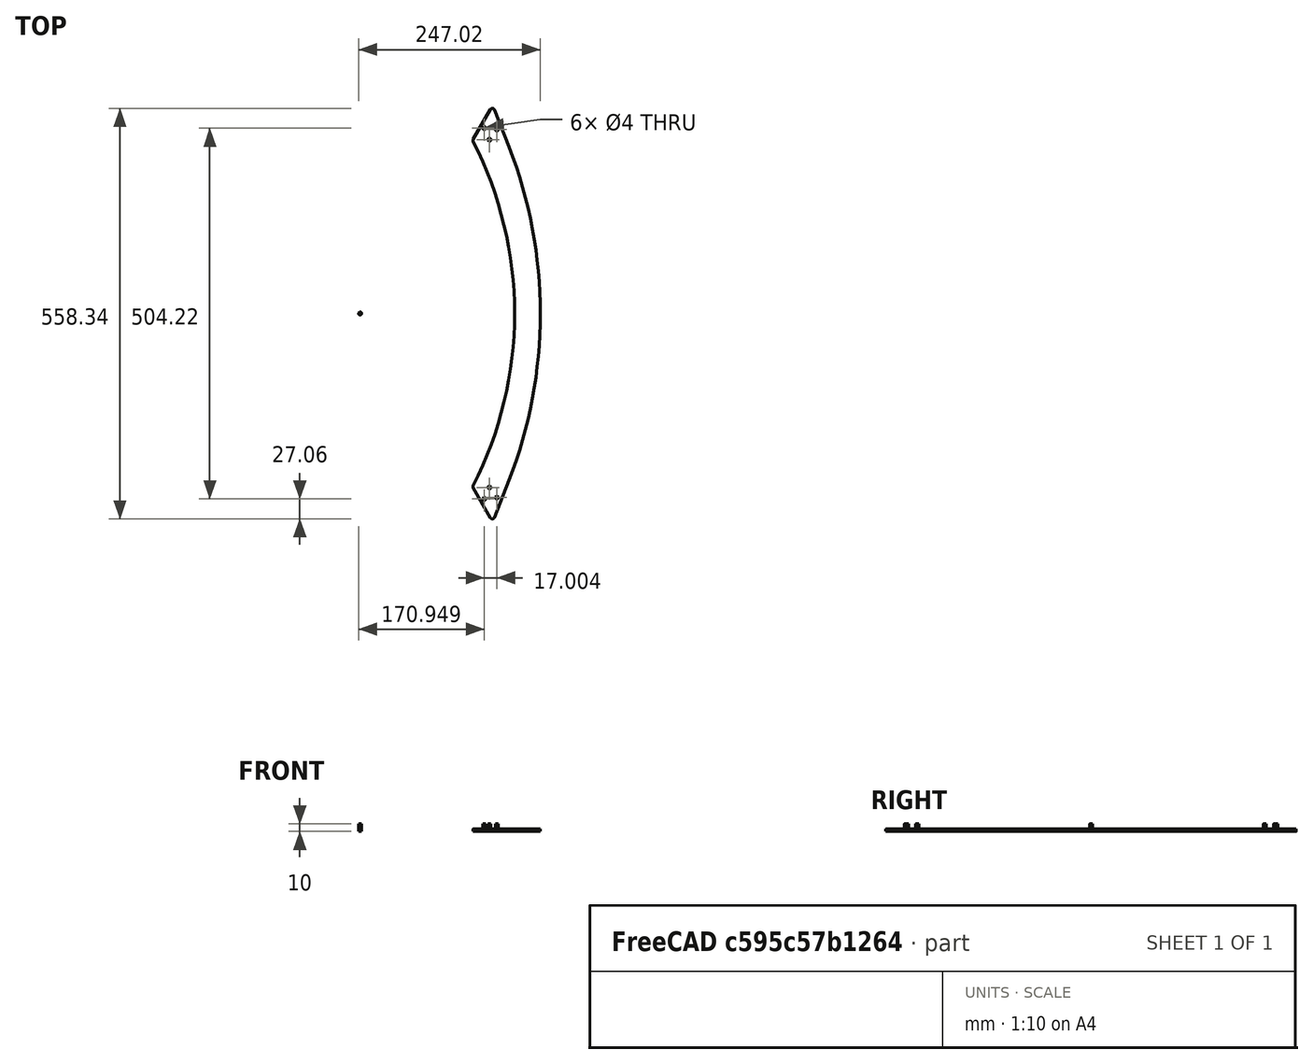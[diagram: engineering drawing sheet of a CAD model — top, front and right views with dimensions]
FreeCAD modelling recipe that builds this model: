
FCSTD DOCUMENT  (FreeCAD 1.1R38827 (Git))
Label: composit_stand3_tech_sector_hor_model
License: All rights reserved
LicenseURL: http://en.wikipedia.org/wiki/All_rights_reserved
objects: Part::FeaturePython×5, App::Link×3, PartDesign::SubShapeBinder×2, PartDesign::Body×2, PartDesign::CoordinateSystem×2, Part::Mirroring×1, PartDesign::Pad×1, Part::Cylinder×1, Part::MultiFuse×1, PartDesign::Boolean×1
note: 19 computed .brp shape members not serialized (recipe doc carries the construction recipe); baked Part::Feature solids carry a one-line shape summary decoded from their .brp
EXTERNAL_REF file=composit_stand3_tech_sector_hor_main.FCStd obj=Sketch
EXTERNAL_REF file=composit_stand3_tech_sector_plexiglass_main.FCStd obj=Placment
EXTERNAL_REF file=composit_stand3_tech_sector_hor_main.FCStd obj=Link001
EXTERNAL_REF file=composit_stand3_tech_sector_pillar_main.FCStd obj=ArrayFromShape

FEATURE [PartDesign::SubShapeBinder] Binder
  BindCopyOnChange = 0
  BindMode = 0
  ClaimChildren = true
  Fuse = false
  MakeFace = true
  OffsetFill = false
  OffsetIntersection = false
  OffsetJoinType = 0
  OffsetOpenResult = false
  PartialLoad = false
  Relative = true
  Support = -> [<external composit_stand3_tech_sector_hor_main.FCStd>#Sketch]
  _Version = 2
FEATURE [Part::Mirroring] Part__Mirroring  label="Binder (Mirror #1)"
  Base = (0,0,0)
  Normal = (0,1,0)
  Source = -> Binder
FEATURE [Part::FeaturePython] Connect  # WARN: FeaturePython — macro-defined, semantics opaque (R4)
  Objects = -> [Binder,Part__Mirroring]
  Tolerance = 0
FEATURE [PartDesign::SubShapeBinder] Binder001
  BindCopyOnChange = 0
  BindMode = 0
  ClaimChildren = true
  Context = -> Body [Binder001.]
  Fuse = false
  MakeFace = true
  OffsetFill = false
  OffsetIntersection = false
  OffsetJoinType = 0
  OffsetOpenResult = false
  PartialLoad = false
  Relative = false
  Support = -> [Connect]
  _Version = 2
FEATURE [PartDesign::Pad] Pad
  Direction = (0,0,1)
  Length = 3
  Length2 = 10
  Profile = -> Binder001
  Suppressed = false
  Type = 0
FEATURE [App::Link] Link001  label="edge_placement"
  LinkTransform = true
  LinkedObject = -> <external composit_stand3_tech_sector_plexiglass_main.FCStd>#Placment
FEATURE [App::Link] Link002  label="front_support_intersection_placement"
  LinkedObject = -> <external composit_stand3_tech_sector_hor_main.FCStd>#Link001
FEATURE [App::Link] Link003  label="holes_bottom"
  LinkedObject = -> <external composit_stand3_tech_sector_pillar_main.FCStd>#ArrayFromShape
FEATURE [Part::FeaturePython] Populate  label="Populate edge_placement with holes"  # WARN: FeaturePython — macro-defined, semantics opaque (R4)
  Copying = 0
  ExposePlacement = false
  MarkerShape = 1
  MarkerSize = 0
  NumElements = 3
  Object = -> Link003
  OutputCompounding = 0
  PlacementsFrom = -> Link002
  PlacementsTo = -> Link001
  Referencing = 3
  Type = lattice2PopulateCopies.LatticePopulateCopies
  isLattice = 1
FEATURE [Part::FeaturePython] Mirror  label="Mirror of Populate edge_placement with holes"  # WARN: FeaturePython — macro-defined, semantics opaque (R4)
  ExposePlacement = false
  FlipX = false
  FlipY = true
  FlipZ = false
  MarkerShape = 1
  MarkerSize = 0
  NumElements = 3
  Object = -> Populate
  ObjectTraversal = 0
  Type = lattice2Mirror.LatticeMirror
  isLattice = 1
FEATURE [Part::FeaturePython] Join  # WARN: FeaturePython — macro-defined, semantics opaque (R4)
  ExposePlacement = false
  Interleave = false
  Links = -> [Populate,Mirror]
  MarkerShape = 1
  MarkerSize = 0
  NumElements = 6
  Type = lattice2JoinArrays.JoinArrays
  isLattice = 1
FEATURE [Part::Cylinder] Cylinder  label="hole_3.4mm"
  Angle = 360
  AttacherType = Attacher::AttachEngine3D
  FirstAngle = 0
  Height = 10
  Radius = 2
  SecondAngle = 0
FEATURE [Part::FeaturePython] Populate001  label="Populate Join with hole_3.4mm"  # WARN: FeaturePython — macro-defined, semantics opaque (R4)
  Copying = 0
  ExposePlacement = false
  MarkerShape = 1
  MarkerSize = 0
  NumElements = 0
  Object = -> Cylinder
  OutputCompounding = 1
  PlacementsTo = -> Join
  Referencing = 0
  Type = lattice2PopulateCopies.LatticePopulateCopies
  isLattice = 0
FEATURE [PartDesign::Body] Body001
  AllowCompound = false
  Origin = -> Origin001
FEATURE [Part::MultiFuse] Fusion
  Shapes = -> [Populate001]
FEATURE [PartDesign::Boolean] Boolean
  BaseFeature = -> Pad
  Group = -> [Fusion]
  Suppressed = false
  Type = 1
  UsePlacement = true
FEATURE [PartDesign::CoordinateSystem] Local_CS  label="base_LCS"
  AttacherType = Attacher::AttachEngine3D
  AttachmentSupport = -> [XY_Plane]
  MapMode = 5
FEATURE [PartDesign::CoordinateSystem] Local_CS001  label="pillar_LCS"
  AttacherType = Attacher::AttachEngine3D
  AttachmentOffset = pos=(180.364,283.047,3) rot=(0,0,1;1.94804rad)
  AttachmentSupport = -> [XY_Plane]
  MapMode = 5
  Placement = pos=(180.364,283.047,3) rot=(0,0,1;1.94804rad)
  expr: AttachmentOffset = placement(vector(0; 0; 3); rotation(0; 0; 0)) * <<edge_placement>>.LinkedObject.Placement
FEATURE [PartDesign::Body] Body  label="hor"
  AllowCompound = false
  Group = -> [Binder001,Pad,Boolean,Local_CS,Local_CS001]
  Origin = -> Origin
  Tip = -> Boolean

RESOLVED EXTERNAL PARTS (link-assembly join: the EXTERNAL_REF files above that resolve inside this repo's crawl, each included once):
---- part composit_stand3_tech_sector_hor_main.FCStd = doc fcstd_1353915c5591 ----
FCSTD DOCUMENT  (FreeCAD 1.1R38827 (Git))
Label: composit_stand3_tech_sector_hor_main
License: All rights reserved
LicenseURL: http://en.wikipedia.org/wiki/All_rights_reserved
objects: PartDesign::SubShapeBinder×2, App::Link×2, Part::FeaturePython×1, Sketcher::SketchObject×1
note: 5 computed .brp shape members not serialized (recipe doc carries the construction recipe); baked Part::Feature solids carry a one-line shape summary decoded from their .brp
EXTERNAL_REF file=composit_stand3_tech_sector_plexiglass_main.FCStd obj=Sketch
EXTERNAL_REF file=composit_stand3_tech_sector_pillar_main.FCStd obj=Sketch
EXTERNAL_REF file=composit_stand3_tech_sector_plexiglass_main.FCStd obj=Placment
EXTERNAL_REF file=composit_stand3_tech_sector_pillar_main.FCStd obj=Placment

FEATURE [PartDesign::SubShapeBinder] Binder
  BindCopyOnChange = 0
  BindMode = 0
  ClaimChildren = false
  Fuse = false
  MakeFace = true
  OffsetFill = false
  OffsetIntersection = false
  OffsetJoinType = 0
  OffsetOpenResult = false
  PartialLoad = false
  Relative = true
  Support = -> [<external composit_stand3_tech_sector_plexiglass_main.FCStd>#Sketch]
  _Version = 2
FEATURE [PartDesign::SubShapeBinder] Binder001
  BindCopyOnChange = 0
  BindMode = 0
  ClaimChildren = false
  Fuse = false
  MakeFace = true
  OffsetFill = false
  OffsetIntersection = false
  OffsetJoinType = 0
  OffsetOpenResult = false
  PartialLoad = false
  Relative = true
  Support = -> [<external composit_stand3_tech_sector_pillar_main.FCStd>#Sketch]
  _Version = 2
FEATURE [App::Link] Link  label="edge_placement"
  LinkTransform = true
  LinkedObject = -> <external composit_stand3_tech_sector_plexiglass_main.FCStd>#Placment
FEATURE [App::Link] Link001  label="front_support_intersection_placement"
  LinkTransform = true
  LinkedObject = -> <external composit_stand3_tech_sector_pillar_main.FCStd>#Placment
FEATURE [Part::FeaturePython] Populate  label="Populate edge_placement with Binder001"  # WARN: FeaturePython — macro-defined, semantics opaque (R4)
  Copying = 0
  ExposePlacement = false
  MarkerShape = 1
  MarkerSize = 0
  NumElements = 0
  Object = -> Binder001
  OutputCompounding = 2
  PlacementsFrom = -> Link001
  PlacementsTo = -> Link
  Referencing = 3
  Type = lattice2PopulateCopies.LatticePopulateCopies
  isLattice = 0
FEATURE [Sketcher::SketchObject] Sketch
  ArcFitTolerance = 0
  ExternalGeometry = -> [Binder,Populate]
  FullyConstrained = true
  MakeInternals = false
  sketch-geometry (6):
    g0: ArcOfCircle CenterX=-383.193 CenterY=0 CenterZ=0 NormalX=0 NormalY=0 NormalZ=1 AngleXU=0 Radius=628.213 StartAngle=0 EndAngle=0.369284
    g1: ArcOfCircle CenterX=179.86 CenterY=276.175 CenterZ=0 NormalX=0 NormalY=0 NormalZ=1 AngleXU=0 Radius=3 StartAngle=0.377243 EndAngle=2.61799
    g2: ArcOfCircle CenterX=156.28 CenterY=235.332 CenterZ=0 NormalX=0 NormalY=0 NormalZ=1 AngleXU=0 Radius=3 StartAngle=2.61799 EndAngle=3.61477
    g3: ArcOfCircle CenterX=-303.381 CenterY=0 CenterZ=0 NormalX=0 NormalY=0 NormalZ=1 AngleXU=0 Radius=513.4 StartAngle=0 EndAngle=0.473178
    g4: LineSegment StartX=202.67 StartY=226.752 StartZ=0 EndX=182.65 EndY=277.28 EndZ=0
    g5: LineSegment StartX=153.682 StartY=236.832 StartZ=0 EndX=177.262 EndY=277.675 EndZ=0
  constraints (18):
    c: PointOnObject(g0,g-1)
    c: PointOnObject(g0,g-1)
    c: PointOnObject(g-3,g0)
    c: Coincident(g0,g-3)
    c: PointOnObject(g3,g-1)
    c: PointOnObject(g3,g-1)
    c: Coincident(g4,g0)
    c: Tangent(g4,g-3)
    c: Tangent(g4,g1) = -1.5708
    c: Tangent(g3,g2) = 1.5708
    c: Tangent(g5,g2) = 1.5708
    c: Tangent(g5,g1) = 1.5708
    c: PointOnObject(g-4,g5)
    c: PointOnObject(g2,g-4)
    c: Equal(g1,g2)
    c: Radius(g1) = 3
    c: PointOnObject(g-4,g3)
    c: DistanceX(g3,g0) = 35
---- part composit_stand3_tech_sector_plexiglass_main.FCStd = doc fcstd_4438cd22ccd8 ----
FCSTD DOCUMENT  (FreeCAD 1.1R38827 (Git))
Label: composit_stand3_tech_sector_plexiglass_main
License: All rights reserved
LicenseURL: http://en.wikipedia.org/wiki/All_rights_reserved
objects: Part::FeaturePython×2, Sketcher::SketchObject×1, Part::Feature×1
note: 5 computed .brp shape members not serialized (recipe doc carries the construction recipe); baked Part::Feature solids carry a one-line shape summary decoded from their .brp
EXTERNAL_REF file=composit_stand3_tech_sector_pillar_main.FCStd obj=Sketch

FEATURE [Sketcher::SketchObject] Sketch  label="main_sketch"
  ArcFitTolerance = 0
  FullyConstrained = true
  MakeInternals = false
  expr: .Constraints.angle = 60 deg + <<composit_stand3_tech_sector_pillar_main>>#<<Sketch>>.Constraints.angle
  expr: Constraints[5] = <<composit_stand3_tech_sector_pillar_main>>#<<Sketch>>.Constraints.front
  sketch-geometry (3):
    g0: LineSegment StartX=202.67 StartY=226.752 StartZ=0 EndX=180.364 EndY=283.047 EndZ=0
    g1: ArcOfCircle CenterX=-357 CenterY=5 CenterZ=0 NormalX=0 NormalY=0 NormalZ=1 AngleXU=0 Radius=602 StartAngle=0 EndAngle=0.377243
    g2: LineSegment StartX=245 StartY=5 StartZ=0 EndX=245 EndY=0 EndZ=0
  constraints (9):
    c: Angle(g0) = 1.94804  'angle'
    c: Tangent(g0,g1) = -1.5708
    c: Vertical(g2)
    c: Tangent(g2,g1) = 1.5708
    c: DistanceY(g2,g2) = 5
    c: Distance(g0) = 60.5533
    c: PointOnObject(g2,g-1)
    c: Radius(g1) = 602  'r'
    c: DistanceX(g2) = 245  'offset'
FEATURE [Part::Feature] Body160  label="tech_sector_plexiglass_material_0.30ansi001"
  Placement = pos=(0,0,0) rot=(0,0,-1;0.523599rad)
  shape: bbox 73.31 x 566.4 x 419 mm, 26 faces (baked)
FEATURE [Part::FeaturePython] Placment  label="edge_placement"  # WARN: FeaturePython — macro-defined, semantics opaque (R4)
  AttacherType = Attacher::AttachEngine3D
  AttachmentOffset = pos=(0,0,0) rot=(-0.57735,0.57735,0.57735;2.0944rad)
  AttachmentSupport = -> [Sketch]
  ExposePlacement = true
  MapMode = 7
  MarkerShape = 1
  MarkerSize = 50
  NumElements = 1
  Placement = pos=(180.364,283.047,0) rot=(0,0,1;1.94804rad)
  Type = lattice2AttachablePlacement.AttachablePlacement
  isLattice = 1
FEATURE [Part::FeaturePython] Placment001  label="fix_corner_placement"  # WARN: FeaturePython — macro-defined, semantics opaque (R4)
  AttacherType = Attacher::AttachEngine3D
  ExposePlacement = true
  MarkerShape = 1
  MarkerSize = 200
  NumElements = 1
  Placement = pos=(245,0,3) rot=(0,0,1;1.5708rad)
  Type = lattice2AttachablePlacement.AttachablePlacement
  isLattice = 1
  expr: .Placement.Base.x = <<main_sketch>>.Constraints.offset
